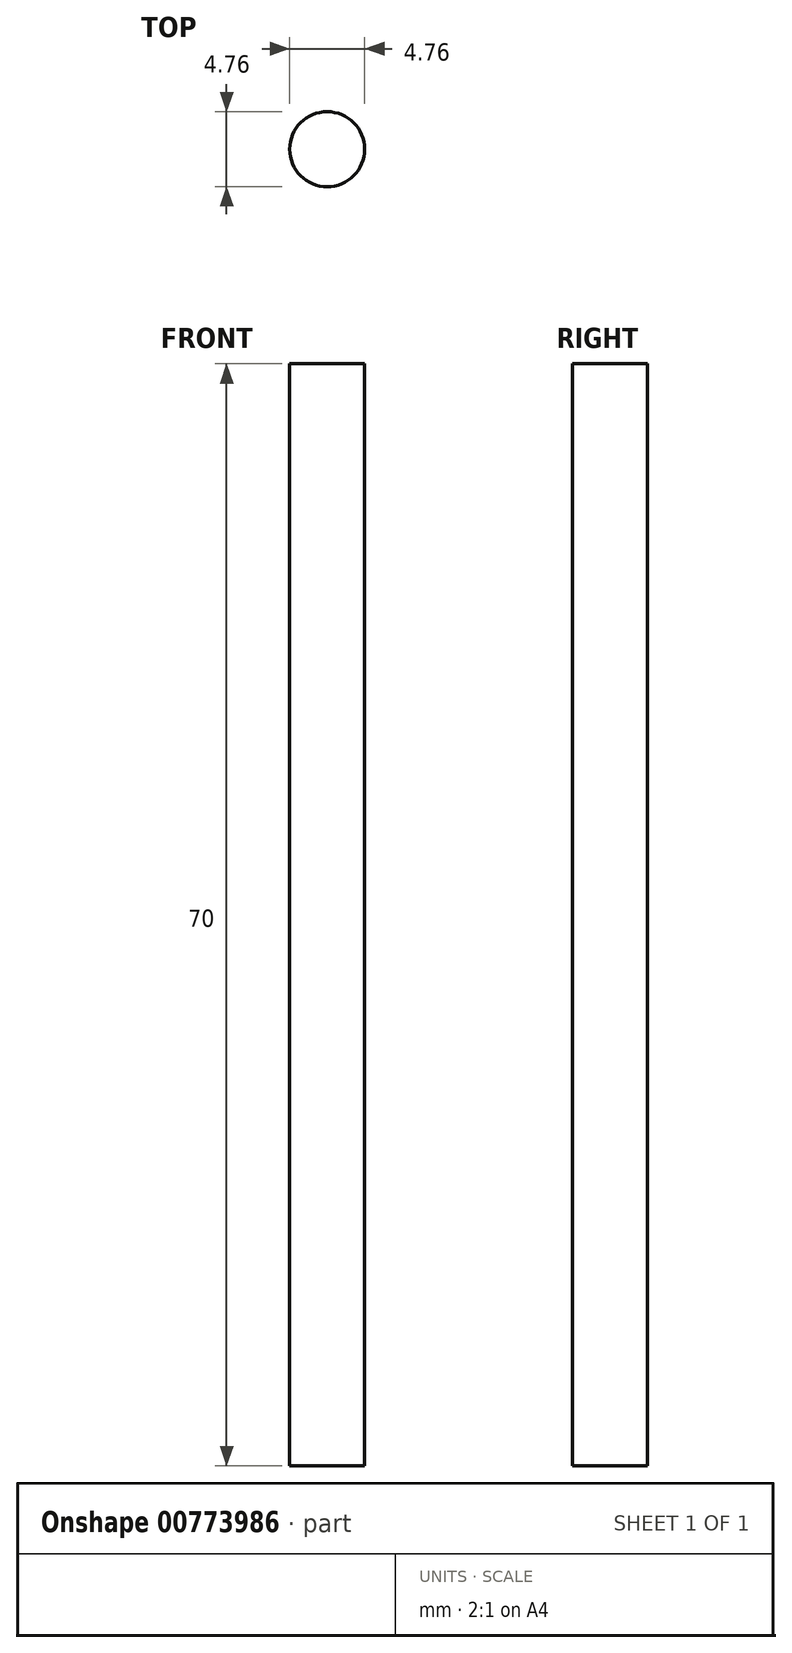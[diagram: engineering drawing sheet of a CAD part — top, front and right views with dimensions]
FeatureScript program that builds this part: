
annotation { "Feature Type Name" : "Feature", "Feature Type Description" : "" }
export const myFeature = defineFeature(function(context is Context, id is Id, definition is map)
    precondition{}
    {
        {
            var Q0;
            Q0=qCreatedBy(makeId("Top.planeOp"),FACE);
            var sketch = newSketch(context, id + "F0", { "sketchPlane" : qUnion([Q0])});
            skCircle(sketch, "E0", {"center": v(0, 0) * mm, "radius": 2.38 * mm});
            skSolve(sketch);
        }
        {
            var Q0;
            Q0=makeQuery(id+"F0.imprint","IMPRINT",FACE,{"disambiguationData":[TD([[makeQuery(id+"F0.imprint","IMPRINT",EDGE,{"derivedFrom":sQuery(id+"F0.wireOp",EDGE,"E0")}),1.0]])]});
            extrude(context, id + "F1", {"entities" : qUnion([Q0]), "depth" : 70 * mm, "offsetDistance" : 25 * mm});
        }
    });
